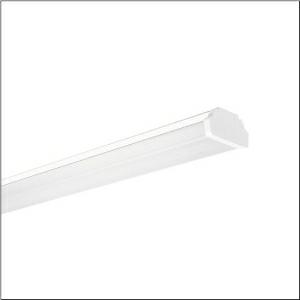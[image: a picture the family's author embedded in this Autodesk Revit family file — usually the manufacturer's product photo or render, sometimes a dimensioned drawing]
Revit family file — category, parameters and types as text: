
# Revit family: dus_31_gen_2_53bd813dv4dxd2_11a4
name_source: partatom
category: Lighting Fixtures
units: mm (PartAtom-declared; Revit-internal decimal feet)

## family parameters
Cut with Voids When Loaded = No
Host = Face
Light Source = No
Part Type = Normal
Room Calculation Point = No
Round Connector Dimension = Use Diameter
Shared = No

## types (1)
- --- (1 x LED, 13370 lm, 74.9 W, 4000K)
    Apparent Load = 75 VA
    CIE Flux Codes = 62 83 95 93 100
    Color Rendering = 80
    Color Temperature = 4000K
    Default Elevation = 1800 mm
    Description = DUS 31 Gen.2, luminaire insert, of sheet steel, coil coated, white, length: 1.535mm, width: 81mm, height: 90mm, 5x system unit, system units: 307mm, LED rated luminous flux: 13.370lm, light colour: 840, SDCM (Standard Deviation of Colour Matching)MacAdam ≤ 3 SDCM (initial), control gear: DALI 2, control gear: ECG DALI, with plug, 5-pole, with phase selection, mains connection: 220..240V, AC, 50/60Hz, rated input power: 75W, through-wiring accessed according to module size, primary optical cover: cover, of PMMA, light emission: direct distribution, primary light characteristic: symmetric, protection rating (complete): IP20, protection rating (LED compartment): IP50, insulation class (complete): insulation class I (protective earthing), certification: CE, ENEC, VDE, UKCA, impact resistance: IK03, permissible ambient temperature for indoor applications: -25..+35°C, corresponds to IFS (International Featured Standards) requirements for safety and quality in the food industry, reducing of maximum allowable ambient temperature of 5°C with ceiling mounting, packaging unit: 1 piece
    Height = 95 mm
    Lamp = 1 x LED
    Lamp Light Flux = 13370 lm
    Lamp Power = 74.9 W
    Lamp count = 1
    Length = 1535 mm
    Luminous efficacy = 179 lm/W
    Manufacturer = Siteco
    ModVariant = No
    Model = 53BD813DV4DXD2
    Mounting Place = Ceiling
    Mounting Type = Pendant
    Number of Poles = 1
    OnlyDefault = Yes
    Power Factor = 1
    Product Name = DUS 31 Gen.2
    Product group = luminaire insert | ceiling pendant
    ProductGroupID = 901
    Protection Class = Protection class I
    Protection Degree = IP 20
    RLX_Detail_Level = 1
    RLX_Emergency_Light_Flux = 0 lm
    RLX_Emergency_Type = 0
    RLX_Emergency_Type_DB = No
    RlxData = <blob elided: 32469 chars, md5=8ee074dd>
    Socket = socket
    Standby Power = 0 W
    System Light Flux = 13370 lm
    System Power = 75 W
    Type Comments = factory setting: luminous flux: 100 % | dim-lin: 254 | 511 mA
    Type Image = l_1319596.jpg
    URL = http://relux.com
    VarID = @adj_050263
    Voltage = 0 V
    Weight = 0.00 kg
    Width = 81 mm

## geometry (parser evidence)
native form markers: Blend x4, Sweep x13
no freeform markers — native parametric forms only
